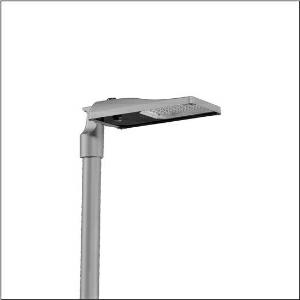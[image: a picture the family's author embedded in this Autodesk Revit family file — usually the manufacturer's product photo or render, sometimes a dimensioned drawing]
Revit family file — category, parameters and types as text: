
# Revit family: streetlight_sl_31_mini___p0_8a_5xh6u31t08ga_f82c
name_source: partatom
category: Lighting Fixtures
units: mm (PartAtom-declared; Revit-internal decimal feet)

## family parameters
Cut with Voids When Loaded = No
Host = Face
Light Source = No
Part Type = Normal
Room Calculation Point = No
Round Connector Dimension = Use Diameter
Shared = No

## types (1)
- --- (1 x LED, 5930 lm, 39.3 W, 3000K)
    Apparent Load = 39 VA
    CIE Flux Codes = 33 69 96 100 100
    Color Rendering = 70
    Color Temperature = 3000K
    Default Elevation = 1800 mm
    Description = Streetlight SL 31 mini D4i, Desk-Remote mast luminaire for post-top, side-entry; light control with lens of PMMA; light distribution: P0.8a, direct asymmetric distribution, for standard-compliant lighting for roads and squares; LED: luminous flux: 5.930lm, light colour: 730, colour temperature: 3000K; luminous efficacy: 150,9lm/W; control: pre-setting: logarithmic dimming characteristic, flexible luminous flux parameterisation, time-dependent luminous flux control, constant luminous flux control, power reduction, intelligent temperature release in ECG and LED module, overheat protection; luminaire housing, of diecast aluminium, Siteco® metallic grey (DB 702S), corrosivity category C5 high according to DIN EN ISO 12944; cover of toughened safety glass, transparent, opened without tools; mast flange of diecast aluminium, Siteco® metallic grey (DB 702S), spigot size: 76/60mm, mast flange included unmounted; with cable H07RN-F 2x 1.5mm², cable length: 6,5m, connection cable pre-assembled; mains connection: 220..240V, AC, 50/60Hz; power consumption (at start of service life): 39,3W / (at end of service life): 40,7W / (with reduced operation 50%): 18,1W; protection rating (complete): IP66; insulation class (complete): insulation class II (safety insulation); impact resistance: IK09; certification: CE, ENEC, ENEC+, VDE, UKCA, ZD4i; permissible operating ambient temperature for outdoor applications: -40..+50°C; packaging unit: 1 piece

Light Distribution: P0.8a
    Height = 76 mm
    Lamp = 1 x LED
    Lamp Light Flux = 5930 lm
    Lamp Power = 39.3 W
    Lamp count = 1
    Length = 547 mm
    Luminous efficacy = 151 lm/W
    Manufacturer = Siteco
    ModVariant = No
    Model = 5XH6U31T08GA
    Number of Poles = 1
    OnlyDefault = Yes
    Power Factor = 1
    Product Name = Streetlight SL 31 mini | P0.8a
    Product group = mast luminaire | pylon top
    ProductGroupID = 6100
    Protection Class = Protection class II
    Protection Degree = IP 66
    RLX_Detail_Level = 1
    RLX_Emergency_Light_Flux = 0 lm
    RLX_Emergency_Type = 0
    RLX_Emergency_Type_DB = No
    RlxData = <blob elided: 39721 chars, md5=e859f047>
    Socket = socket
    Standby Power = 0 W
    System Light Flux = 5930 lm
    System Power = 39 W
    Type Comments = factory setting: luminous flux: 100 % | dim-lin: 254 | 798 mA
    Type Image = l_1300332.jpg
    URL = http://relux.com
    VarID = @adj_078997
    Voltage = 0 V
    Weight = 0.00 kg
    Width = 265 mm

## geometry (parser evidence)
native form markers: Blend x4, Sweep x8
no freeform markers — native parametric forms only
